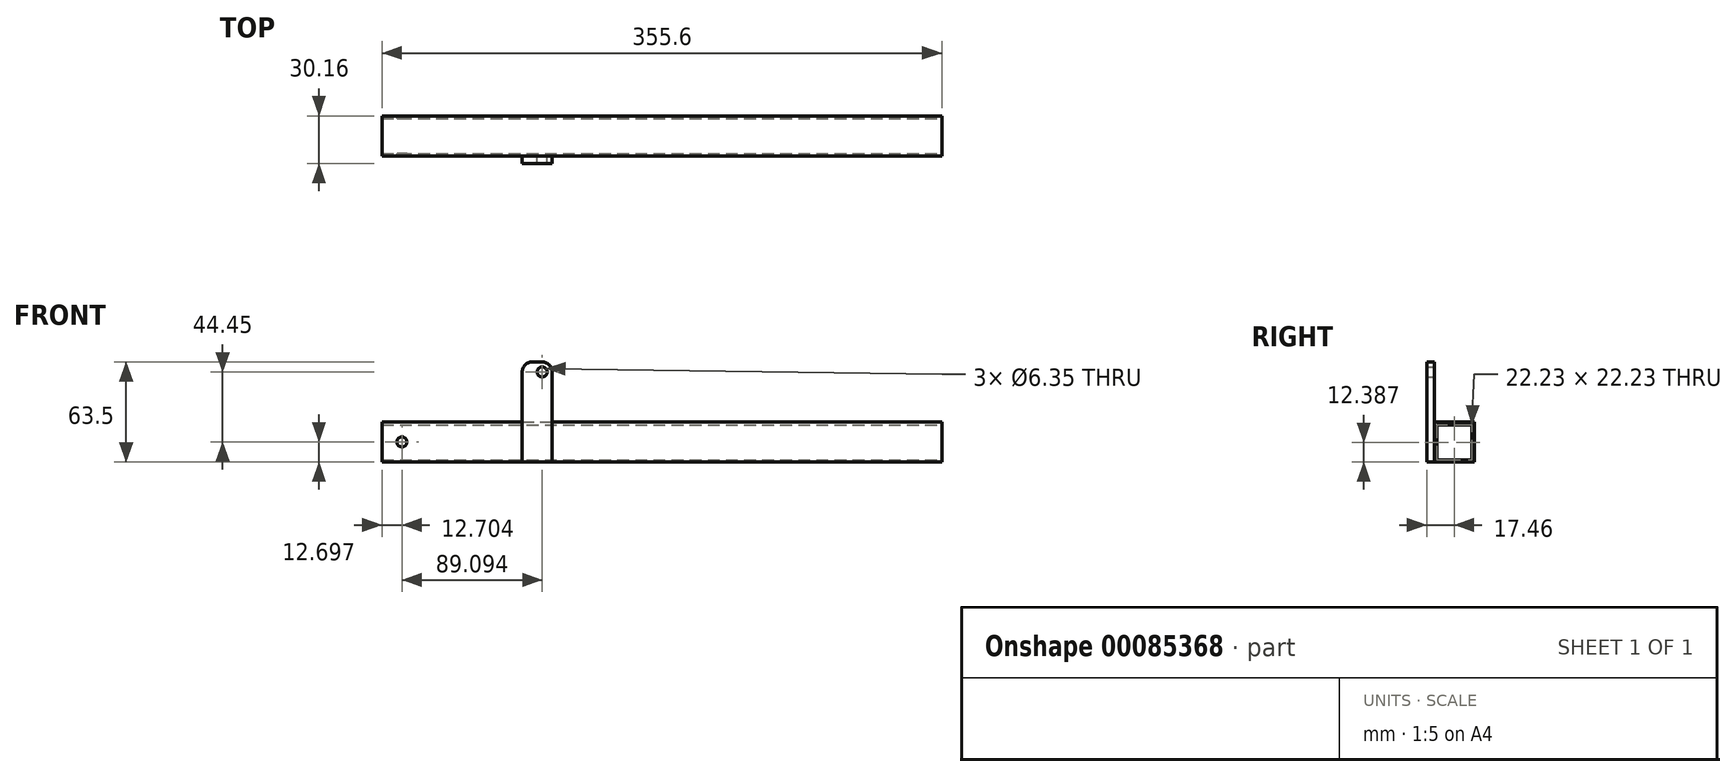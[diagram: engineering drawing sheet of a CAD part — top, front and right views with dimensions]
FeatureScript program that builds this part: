
annotation { "Feature Type Name" : "Feature", "Feature Type Description" : "" }
export const myFeature = defineFeature(function(context is Context, id is Id, definition is map)
    precondition{}
    {
        {
            var Q0;
            Q0=qCreatedBy(makeId("Front.planeOp"),FACE);
            var sketch = newSketch(context, id + "F0", { "sketchPlane" : qUnion([Q0])});
            skLineSegment(sketch, "E0.bottom", {"start": v(-203.66, 1.9) * mm, "end": v(151.94, 1.9) * mm});
            skLineSegment(sketch, "E0.top", {"start": v(-203.66, -23.5) * mm, "end": v(151.94, -23.5) * mm});
            skLineSegment(sketch, "E0.left", {"start": v(-203.66, 1.9) * mm, "end": v(-203.66, -23.5) * mm});
            skLineSegment(sketch, "E0.right", {"start": v(151.94, 1.9) * mm, "end": v(151.94, -23.5) * mm});
            skCircle(sketch, "E1", {"center": v(-190.96, -10.8) * mm, "radius": 3.18 * mm});
            skSolve(sketch);
        }
        {
            var Q0;
            Q0=makeQuery(id+"F0.imprint","IMPRINT",FACE,{"disambiguationData":[TD([[makeQuery(id+"F0.imprint","IMPRINT",EDGE,{"derivedFrom":sQuery(id+"F0.wireOp",EDGE,"E0.bottom")}),-1.0]])]});
            extrude(context, id + "F1", {"entities" : qUnion([Q0]), "depth" : 25.4 * mm});
        }
        {
            var Q0;
            Q0=makeQuery(id+"F1.opExtrude","SWEPT_FACE",FACE,{"disambiguationData":[OSD([sQuery(id+"F0.wireOp",EDGE,"E0.right")])]});
            var sketch = newSketch(context, id + "F2", { "sketchPlane" : qUnion([Q0])});
            skLineSegment(sketch, "E2.bottom", {"start": v(-23.81, 0) * mm, "end": v(-1.59, 0) * mm});
            skLineSegment(sketch, "E2.top", {"start": v(-23.81, -22.23) * mm, "end": v(-1.59, -22.23) * mm});
            skLineSegment(sketch, "E2.left", {"start": v(-23.81, 0) * mm, "end": v(-23.81, -22.23) * mm});
            skLineSegment(sketch, "E2.right", {"start": v(-1.59, 0) * mm, "end": v(-1.59, -22.23) * mm});
            skSolve(sketch);
        }
        {
            var Q0;
            Q0=makeQuery(id+"F2.imprint","IMPRINT",FACE,{"disambiguationData":[TD([[makeQuery(id+"F2.imprint","IMPRINT",EDGE,{"derivedFrom":sQuery(id+"F2.wireOp",EDGE,"E2.bottom")}),-1.0]])]});
            extrude(context, id + "F3", {"entities" : qUnion([Q0]), "operationType" : NewBodyOperationType.REMOVE, "endBound" : BoundingType.THROUGH_ALL, "oppositeDirection" : true, "depth" : 25.4 * mm});
        }
        {
            var Q0;
            Q0=makeQuery(id+"F1.opExtrude","CAP_FACE",FACE,{"disambiguationData":[OSD([sQuery(id+"F0.wireOp",EDGE,"E0.bottom"),sQuery(id+"F0.wireOp",EDGE,"E0.top"),sQuery(id+"F0.wireOp",EDGE,"E0.left"),sQuery(id+"F0.wireOp",EDGE,"E0.right")])],"isStart":false});
            var sketch = newSketch(context, id + "F4", { "sketchPlane" : qUnion([Q0])});
            skLineSegment(sketch, "E3.bottom", {"start": v(-114.56, -23.5) * mm, "end": v(-95.51, -23.5) * mm});
            skLineSegment(sketch, "E3.top", {"start": v(-108.21, 40) * mm, "end": v(-101.86, 40) * mm});
            skLineSegment(sketch, "E3.left", {"start": v(-114.56, -23.5) * mm, "end": v(-114.56, 33.65) * mm});
            skLineSegment(sketch, "E3.right", {"start": v(-95.51, -23.5) * mm, "end": v(-95.51, 33.65) * mm});
            skCircle(sketch, "E4", {"center": v(-101.86, 33.65) * mm, "radius": 3.18 * mm});
            skPoint(sketch, "E5.visualSharp", {"position": v(-114.56, 40) * mm});
            skArc(sketch, "E5.filletArc", {"start": v(-108.21, 40) * mm, "mid": v(-112.7, 38.14) * mm, "end": v(-114.56, 33.65) * mm});
            skPoint(sketch, "E6.visualSharp", {"position": v(-95.51, 40) * mm});
            skArc(sketch, "E6.filletArc", {"start": v(-95.51, 33.65) * mm, "mid": v(-97.37, 38.14) * mm, "end": v(-101.86, 40) * mm});
            skSolve(sketch);
        }
        {
            var Q0;
            Q0=makeQuery(id+"F4.imprint","IMPRINT",FACE,{"disambiguationData":[TD([[makeQuery(id+"F4.imprint","IMPRINT",EDGE,{"derivedFrom":sQuery(id+"F4.wireOp",EDGE,"E3.top")}),-1.0]])]});
            var Q1;
            {var subQ6=sQuery(id+"F4.wireOp",EDGE,"E3.bottom");Q1=makeQuery(id+"F4.imprint","IMPRINT",FACE,{"disambiguationData":[TD([[makeQuery(id+"F4.imprint","IMPRINT",EDGE,{"derivedFrom":subQ6}),1.0]])]});}
            extrude(context, id + "F5", {"entities" : qUnion([Q0, Q1]), "depth" : 4.76 * mm});
        }
    });
